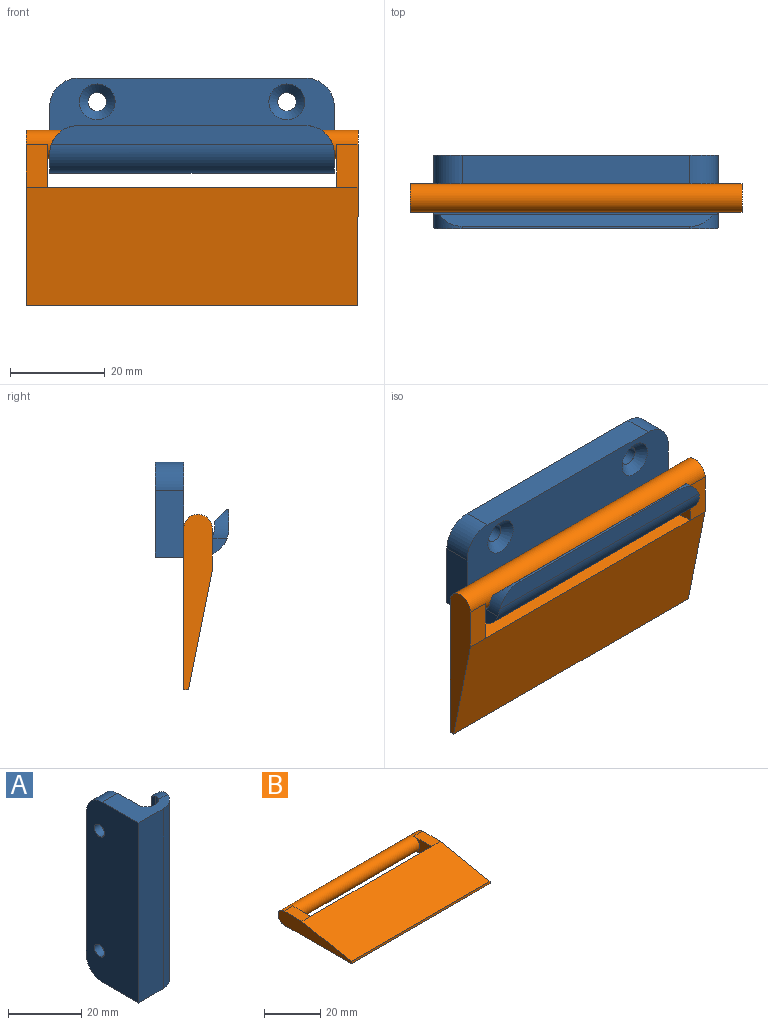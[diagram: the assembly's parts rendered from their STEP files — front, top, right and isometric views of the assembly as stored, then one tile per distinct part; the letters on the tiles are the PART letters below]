
ASSEMBLY  parts=2 mates=1
PART A: 22 faces, bbox 15.5x20x60 mm
  f0: cylinder r=6mm len=60mm, axis (0,0,-1), area 565mm2, adj f1,f10,f11,f12,f15,f17
  f1: plane 59.31x4mm, normal (1,0,0), area 225mm2, adj f0,f2,f15,f17
  f2: plane 48x0.5mm, normal (0,1,0), area 24mm2, adj f1,f13,f15,f17
  f3: plane 59.31x1.5mm, normal (-1,0,0), area 87.9mm2, adj f4,f13,f15,f17
  f4: cylinder r=3mm len=60mm, axis (0,0,-1), area 282.3mm2, adj f3,f5,f11,f12,f15,f17
  f5: plane 60x0.5mm, normal (0,1,0), area 30mm2, adj f4,f6,f11,f12
  f6: cylinder r=3mm len=60mm, axis (0,0,-1), area 282.7mm2, adj f5,f7,f11,f12
  f7: plane 60x14mm, normal (1,0,0), area 734.6mm2, adj f6,f8,f11,f12,f14,f16,f20,f21
  f8: plane 48x6mm, normal (0,1,0), area 288mm2, adj f7,f9,f14,f16
  f9: plane 60x20mm, normal (-1,0,0), area 1160.7mm2, adj f8,f10,f11,f12,f14,f16,f18,f19
  f10: plane 60x9.5mm, normal (0,-1,0), area 570mm2, adj f0,f9,f11,f12
  f11: plane 15.16x14mm, normal (0,0,1), area 111.4mm2, adj f0,f4,f5,f6,f7,f9,f10,f16
  f12: plane 15.16x14mm, normal (0,0,-1), area 111.4mm2, adj f0,f4,f5,f6,f7,f9,f10,f14
  f13: plane 57.75x2.5mm, normal (-0.71,0.71,0), area 193.8mm2, adj f2,f3,f15,f17
  f14: cylinder r=6mm len=6mm, axis (-1,0,0), area 56.5mm2, adj f7,f8,f9,f12
  f15: cylinder r=6mm len=6mm, axis (-1,0,0), area 19.2mm2, adj f0,f1,f2,f3,f4,f12,f13
  f16: cylinder r=6mm len=6mm, axis (1,0,0), area 56.5mm2, adj f7,f8,f9,f11
  f17: cylinder r=6mm len=6mm, axis (1,0,0), area 19.2mm2, adj f0,f1,f2,f3,f4,f11,f13
  f18: cylinder r=1.95mm len=4.17mm, axis (1,0,0), area 51.1mm2, adj f9,f21
  f19: cylinder r=1.95mm len=4.17mm, axis (1,0,0), area 51.1mm2, adj f9,f20
  f20: cone r=1.89mm half-angle=45deg, axis (1,0,0), area 46.7mm2, adj f7,f19
  f21: cone r=1.89mm half-angle=45deg, axis (1,0,0), area 46.7mm2, adj f7,f18
PART B: 11 faces, bbox 70x37x6 mm
  f0: plane 9x4.5mm, normal (0,0,1), area 40.5mm2, adj f1,f2,f9,f10
  f1: plane 9x6mm, normal (1,0,0), area 39.9mm2, adj f0,f6,f8,f9
  f2: plane 37x6mm, normal (-1,0,0), area 155.6mm2, adj f0,f3,f8,f9,f10
  f3: plane 70x1mm, normal (0,-1,0), area 70mm2, adj f2,f4,f8,f10
  f4: plane 37x6mm, normal (1,0,0), area 155.6mm2, adj f3,f7,f8,f9,f10
  f5: plane 9x6mm, normal (-1,0,0), area 39.9mm2, adj f6,f7,f8,f9
  f6: plane 61x6mm, normal (0,1,0), area 366mm2, adj f1,f5,f8,f10
  f7: plane 9x4.5mm, normal (0,0,1), area 40.5mm2, adj f4,f5,f9,f10
  f8: plane 70x34mm, normal (0,0,-1), area 1831mm2, adj f1,f2,f3,f4,f5,f6,f9
  f9: cylinder r=3mm len=70mm, axis (-1,0,0), area 1234.6mm2, adj f0,f1,f2,f4,f5,f7,f8
  f10: plane 70x25mm, normal (0,-0.2,0.98), area 1784.7mm2, adj f0,f2,f3,f4,f6,f7
PLACE A rot(axis=(0.58,-0.58,-0.58),120deg) t=(59.35,15.55,-4)mm
PLACE B rot(axis=(1,0,0),90deg) t=(29.35,9.55,-13.5)mm
MATE revolute B.f9 <-> A.f6  axis (-1,0,0) through (29.35,6.55,2)mm
